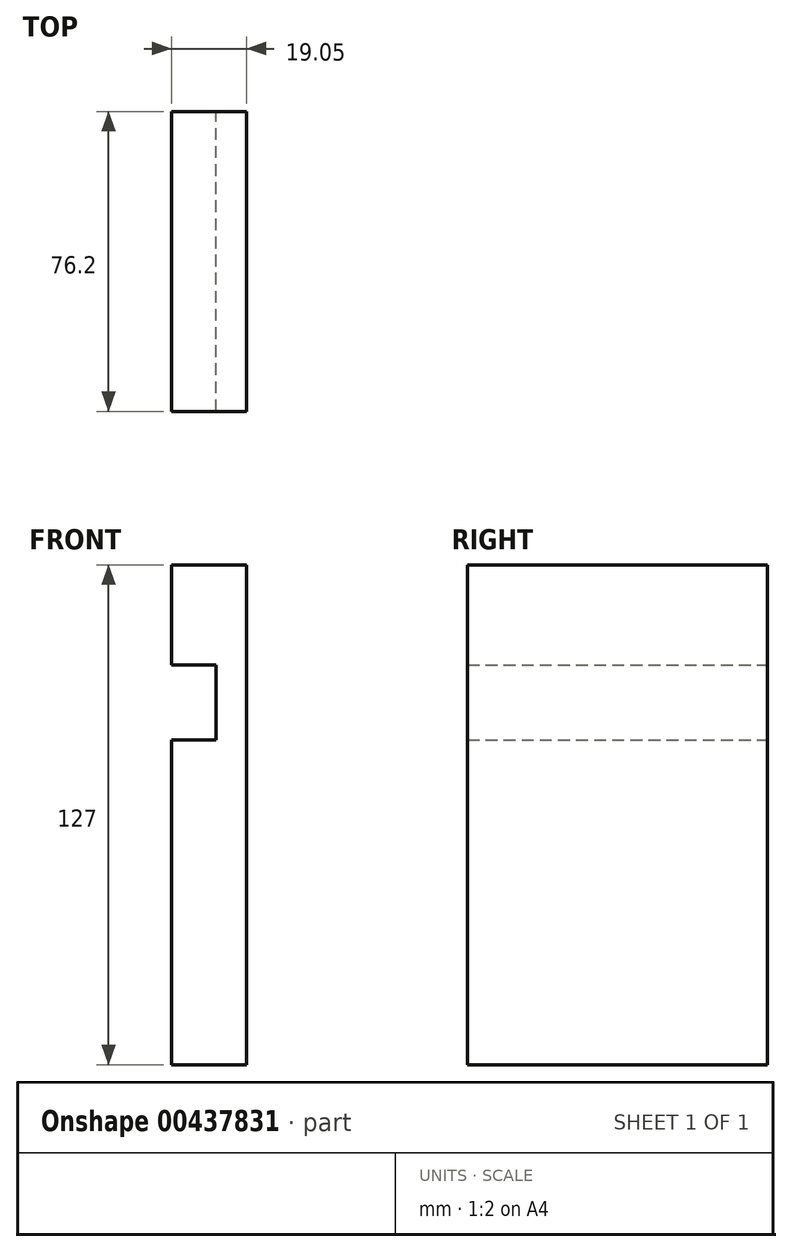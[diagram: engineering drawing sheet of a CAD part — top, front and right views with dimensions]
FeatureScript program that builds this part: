
annotation { "Feature Type Name" : "Feature", "Feature Type Description" : "" }
export const myFeature = defineFeature(function(context is Context, id is Id, definition is map)
    precondition{}
    {
        {
            var Q0;
            Q0=qCreatedBy(makeId("Front.planeOp"),FACE);
            var sketch = newSketch(context, id + "F0", { "sketchPlane" : qUnion([Q0])});
            skLineSegment(sketch, "E0", {"start": v(49.37, -61.5) * mm, "end": v(49.37, 65.5) * mm});
            skLineSegment(sketch, "E1", {"start": v(49.37, 65.5) * mm, "end": v(30.32, 65.5) * mm});
            skLineSegment(sketch, "E2", {"start": v(30.32, 65.5) * mm, "end": v(30.32, 40.1) * mm});
            skLineSegment(sketch, "E3", {"start": v(32.1, 40.1) * mm, "end": v(41.63, 40.1) * mm});
            skLineSegment(sketch, "E4", {"start": v(41.63, 40.1) * mm, "end": v(41.63, 21.05) * mm});
            skLineSegment(sketch, "E5", {"start": v(41.63, 21.05) * mm, "end": v(36.65, 21.05) * mm});
            skLineSegment(sketch, "E6", {"start": v(32.1, 40.1) * mm, "end": v(30.32, 40.1) * mm});
            skLineSegment(sketch, "E7", {"start": v(36.65, 21.05) * mm, "end": v(30.32, 21.05) * mm});
            skLineSegment(sketch, "E8", {"start": v(49.37, -61.5) * mm, "end": v(30.32, -61.5) * mm});
            skLineSegment(sketch, "E9", {"start": v(30.32, -61.5) * mm, "end": v(30.32, 21.05) * mm});
            skSolve(sketch);
        }
        {
            var Q0;
            Q0 = qSketchRegion(id + "F0", true);
            extrude(context, id + "F1", {"entities" : qUnion([Q0]), "depth" : 76.2 * mm});
        }
    });
